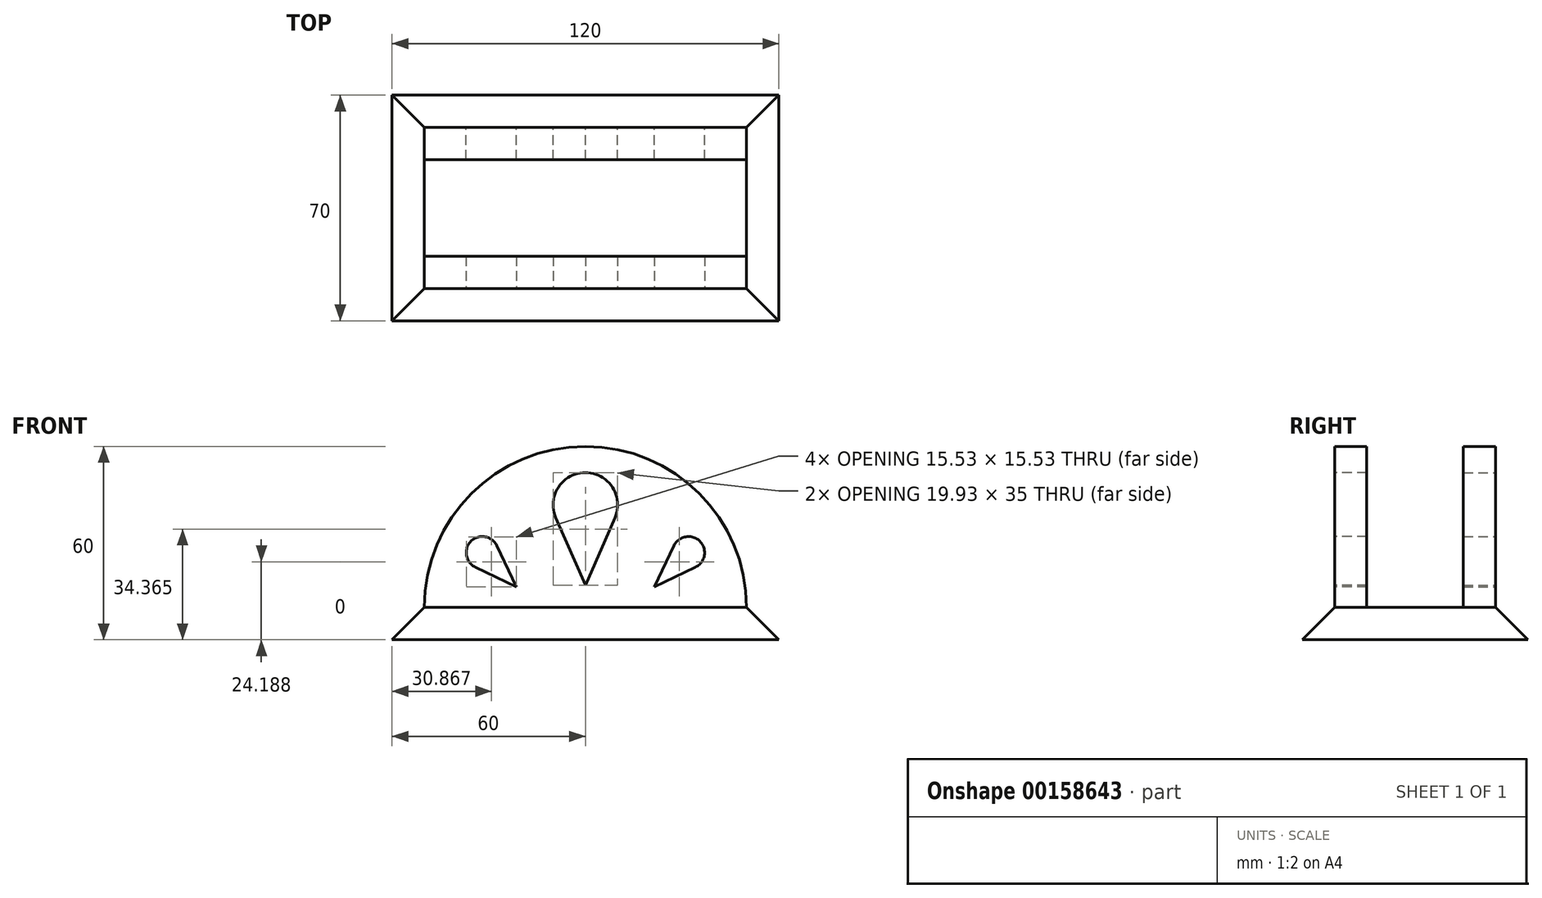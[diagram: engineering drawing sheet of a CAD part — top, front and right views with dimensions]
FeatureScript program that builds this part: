
annotation { "Feature Type Name" : "Feature", "Feature Type Description" : "" }
export const myFeature = defineFeature(function(context is Context, id is Id, definition is map)
    precondition{}
    {
        {
            var Q0;
            Q0=qCreatedBy(makeId("Top.planeOp"),FACE);
            var sketch = newSketch(context, id + "F0", { "sketchPlane" : qUnion([Q0])});
            skLineSegment(sketch, "E0.bottom", {"start": v(60, 35) * mm, "end": v(-60, 35) * mm});
            skLineSegment(sketch, "E0.top", {"start": v(60, -35) * mm, "end": v(-60, -35) * mm});
            skLineSegment(sketch, "E0.left", {"start": v(60, 35) * mm, "end": v(60, -35) * mm});
            skLineSegment(sketch, "E0.right", {"start": v(-60, 35) * mm, "end": v(-60, -35) * mm});
            skPoint(sketch, "E0.middle", {"position": v(0, 0) * mm});
            skSolve(sketch);
        }
        {
            var Q0;
            Q0=qCreatedBy(makeId("Top.planeOp"),FACE);
            cPlane(context, id + "F1", {"entities" : qUnion([Q0]), "cplaneType" : CPlaneType.OFFSET, "offset" : 10 * mm, "width" : 150 * mm, "height" : 150 * mm});
        }
        {
            var Q0;
            Q0=qCreatedBy(id+"F1.planeOp",FACE);
            var sketch = newSketch(context, id + "F2", { "sketchPlane" : qUnion([Q0])});
            skLineSegment(sketch, "E1.bottom", {"start": v(50, -25) * mm, "end": v(-50, -25) * mm});
            skLineSegment(sketch, "E1.top", {"start": v(50, 25) * mm, "end": v(-50, 25) * mm});
            skLineSegment(sketch, "E1.left", {"start": v(50, -25) * mm, "end": v(50, 25) * mm});
            skLineSegment(sketch, "E1.right", {"start": v(-50, -25) * mm, "end": v(-50, 25) * mm});
            skPoint(sketch, "E1.middle", {"position": v(0, 0) * mm});
            skSolve(sketch);
        }
        {
            var Q0;
            Q0=makeQuery(id+"F2.imprint","IMPRINT",FACE,{"disambiguationData":[TD([[makeQuery(id+"F2.imprint","IMPRINT",EDGE,{"derivedFrom":sQuery(id+"F2.wireOp",EDGE,"E1.bottom")}),-1.0]])]});
            var Q1;
            Q1=makeQuery(id+"F0.imprint","IMPRINT",FACE,{"disambiguationData":[TD([[makeQuery(id+"F0.imprint","IMPRINT",EDGE,{"derivedFrom":sQuery(id+"F0.wireOp",EDGE,"E0.bottom")}),1.0]])]});
            loft(context, id + "F3", {"sheetProfilesArray" : [{ "sheetProfileEntities" : qUnion([Q0]) }, { "sheetProfileEntities" : qUnion([Q1]) }]});
        }
        {
            var Q0;
            Q0=qCreatedBy(makeId("Front.planeOp"),FACE);
            cPlane(context, id + "F4", {"entities" : qUnion([Q0]), "cplaneType" : CPlaneType.OFFSET, "offset" : 25 * mm, "oppositeDirection" : true, "width" : 150 * mm, "height" : 150 * mm});
        }
        {
            var Q0;
            Q0=qCreatedBy(id+"F4.planeOp",FACE);
            var sketch = newSketch(context, id + "F5", { "sketchPlane" : qUnion([Q0])});
            skLineSegment(sketch, "E2.bottom", {"start": v(50, 10) * mm, "end": v(-50, 10) * mm});
            skLineSegment(sketch, "E2.top", {"start": v(0, 60) * mm, "end": v(0, 60) * mm});
            skLineSegment(sketch, "E2.left", {"start": v(50, 10) * mm, "end": v(50, 10) * mm});
            skLineSegment(sketch, "E2.right", {"start": v(-50, 10) * mm, "end": v(-50, 10) * mm});
            skPoint(sketch, "E3.visualSharp", {"position": v(-50, 60) * mm});
            skArc(sketch, "E3.filletArc", {"start": v(0, 60) * mm, "mid": v(-35.36, 45.36) * mm, "end": v(-50, 10) * mm});
            skPoint(sketch, "E4.visualSharp", {"position": v(50, 60) * mm});
            skArc(sketch, "E4.filletArc", {"start": v(50, 10) * mm, "mid": v(35.36, 45.36) * mm, "end": v(0, 60) * mm});
            skArc(sketch, "E5", {"start": v(9.17, 37.87) * mm, "mid": v(0, 51.87) * mm, "end": v(-9.17, 37.87) * mm});
            skLineSegment(sketch, "E6", {"start": v(-9.17, 37.87) * mm, "end": v(0, 16.87) * mm});
            skLineSegment(sketch, "E7", {"start": v(0, 16.87) * mm, "end": v(9.17, 37.87) * mm});
            skArc(sketch, "E8", {"start": v(34.13, 22.52) * mm, "mid": v(35.5, 30.56) * mm, "end": v(27.46, 29.18) * mm});
            skLineSegment(sketch, "E9", {"start": v(21.37, 16.42) * mm, "end": v(27.46, 29.18) * mm});
            skLineSegment(sketch, "E10", {"start": v(21.37, 16.42) * mm, "end": v(34.13, 22.52) * mm});
            skLineSegment(sketch, "E11.MirrorCS", {"start": v(-21.37, 16.42) * mm, "end": v(-34.13, 22.52) * mm});
            skLineSegment(sketch, "E12.MirrorCS", {"start": v(-21.37, 16.42) * mm, "end": v(-27.46, 29.18) * mm});
            skArc(sketch, "E13.MirrorCS", {"start": v(-34.13, 22.52) * mm, "mid": v(-35.5, 30.56) * mm, "end": v(-27.46, 29.18) * mm});
            skSolve(sketch);
        }
        {
            var Q0;
            Q0=makeQuery(id+"F5.imprint","IMPRINT",FACE,{"disambiguationData":[TD([[makeQuery(id+"F5.imprint","IMPRINT",EDGE,{"derivedFrom":sQuery(id+"F5.wireOp",EDGE,"E2.bottom")}),-1.0]])]});
            extrude(context, id + "F6", {"entities" : qUnion([Q0]), "operationType" : NewBodyOperationType.ADD, "depth" : 10 * mm});
        }
        {
            var Q0;
            Q0=makeQuery(id+"F3.opLoft","SWEPT_BODY",BODY,{"disambiguationData":[OSD([makeQuery(id+"F0.imprint","IMPRINT",FACE,{"disambiguationData":[TD([[makeQuery(id+"F0.imprint","IMPRINT",EDGE,{"derivedFrom":sQuery(id+"F0.wireOp",EDGE,"E0.bottom")}),1.0]])]}),makeQuery(id+"F2.imprint","IMPRINT",FACE,{"disambiguationData":[TD([[makeQuery(id+"F2.imprint","IMPRINT",EDGE,{"derivedFrom":sQuery(id+"F2.wireOp",EDGE,"E1.bottom")}),-1.0]])]})])]});
            var Q1;
            Q1=qCreatedBy(makeId("Front.planeOp"),FACE);
            mirror(context, id + "F7", {"operationType" : NewBodyOperationType.ADD, "entities" : qUnion([Q0]), "mirrorPlane" : qUnion([Q1])});
        }
    });
